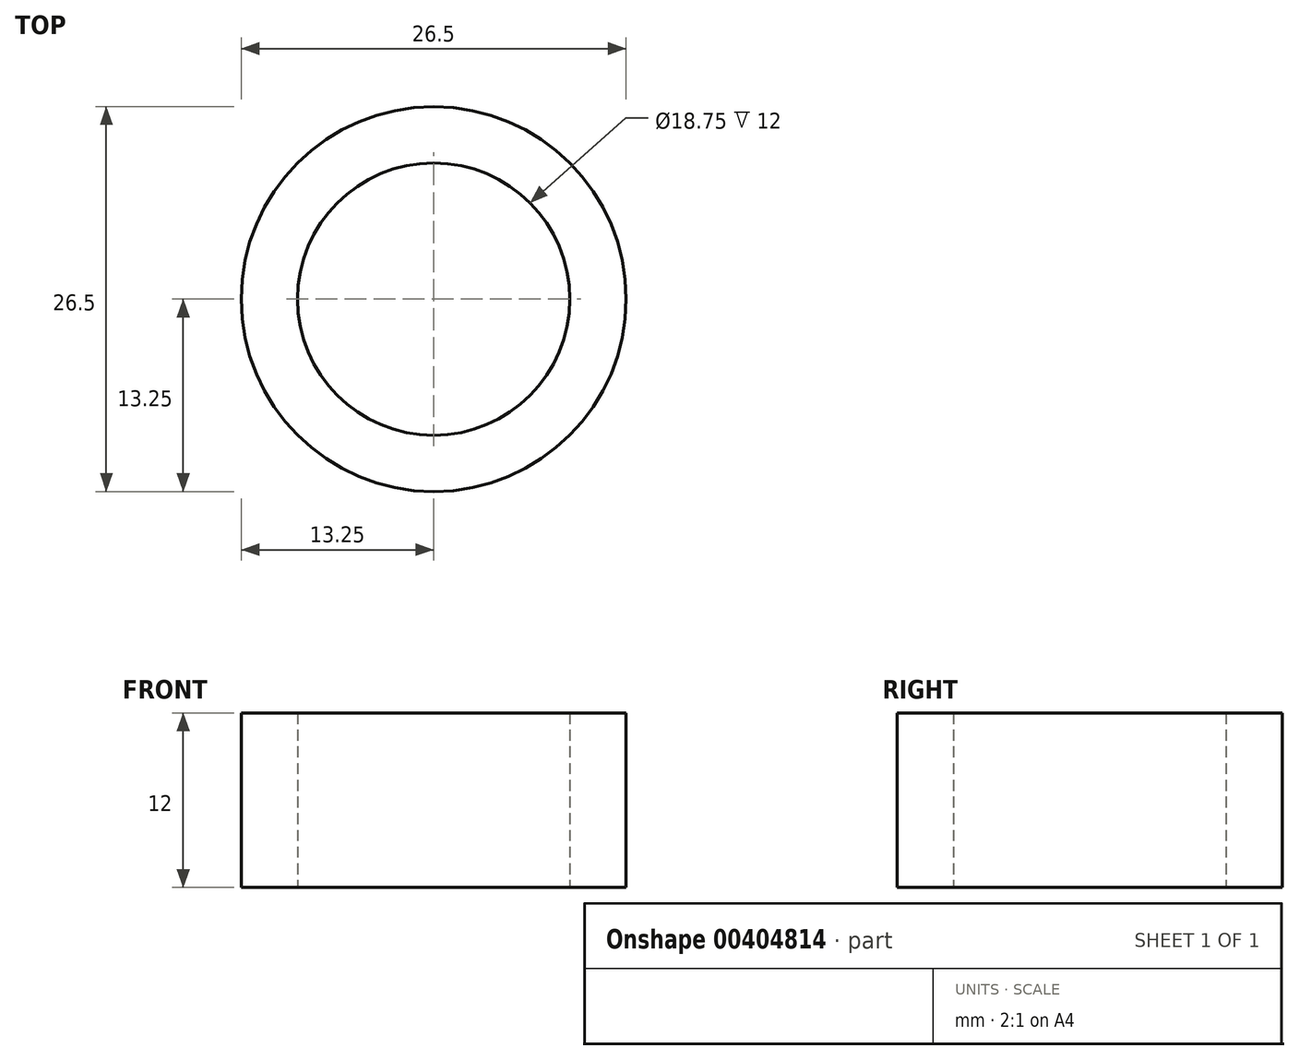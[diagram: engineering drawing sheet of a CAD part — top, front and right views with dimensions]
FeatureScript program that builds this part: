
annotation { "Feature Type Name" : "Feature", "Feature Type Description" : "" }
export const myFeature = defineFeature(function(context is Context, id is Id, definition is map)
    precondition{}
    {
        {
            var Q0;
            Q0=qCreatedBy(makeId("Top.planeOp"),FACE);
            var sketch = newSketch(context, id + "F0", { "sketchPlane" : qUnion([Q0])});
            skCircle(sketch, "E0", {"center": v(0, 0) * mm, "radius": 13.25 * mm});
            skCircle(sketch, "E1", {"center": v(0, 0) * mm, "radius": 9.38 * mm});
            skSolve(sketch);
        }
        {
            var Q0;
            Q0=makeQuery(id+"F0.imprint","IMPRINT",FACE,{"disambiguationData":[TD([[makeQuery(id+"F0.imprint","IMPRINT",EDGE,{"derivedFrom":sQuery(id+"F0.wireOp",EDGE,"E0")}),1.0]])]});
            extrude(context, id + "F1", {"entities" : qUnion([Q0]), "depth" : 12 * mm});
        }
    });
